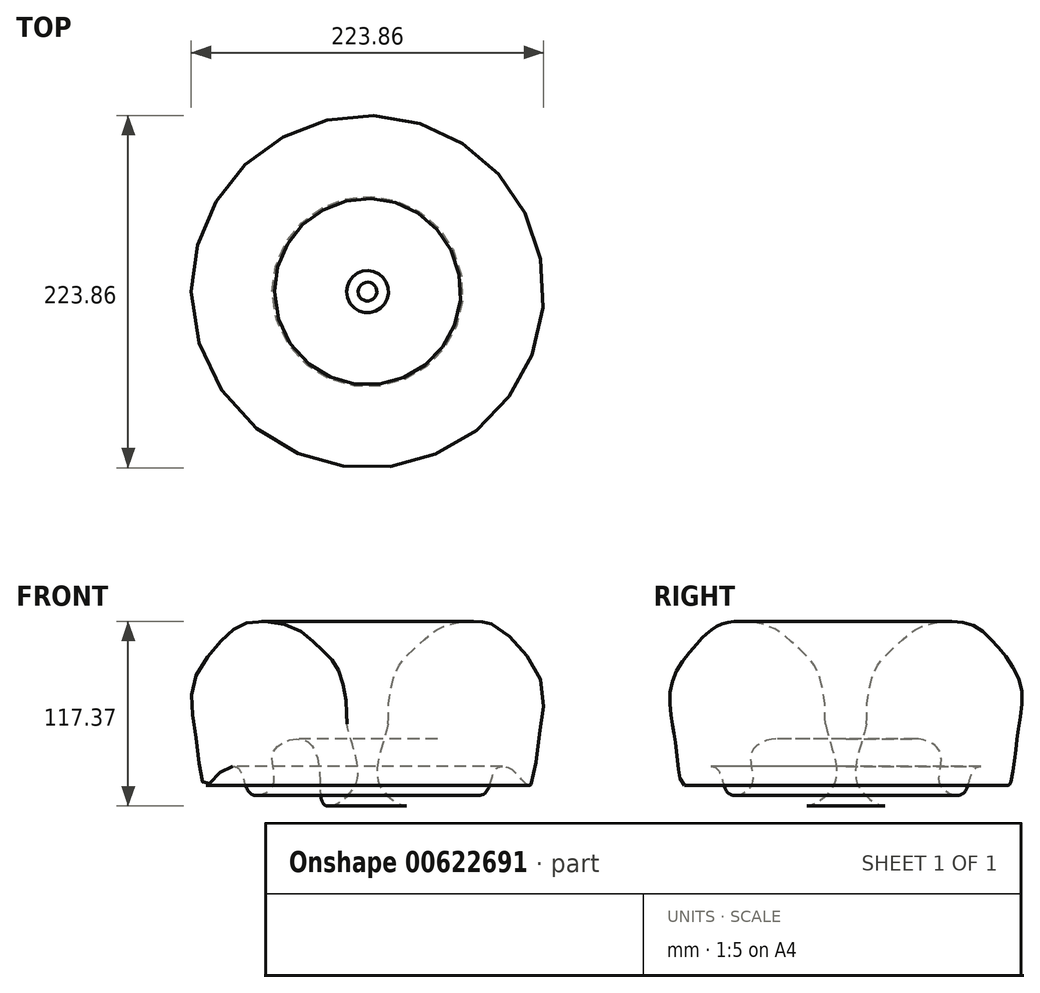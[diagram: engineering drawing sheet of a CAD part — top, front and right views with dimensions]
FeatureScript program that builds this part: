
annotation { "Feature Type Name" : "Feature", "Feature Type Description" : "" }
export const myFeature = defineFeature(function(context is Context, id is Id, definition is map)
    precondition{}
    {
        {
            var Q0;
            Q0=qCreatedBy(makeId("Top.planeOp"),FACE);
            var sketch = newSketch(context, id + "F0", { "sketchPlane" : qUnion([Q0])});
            skCircle(sketch, "E0.cCircle", {"center": v(0, 0) * mm, "radius": 44.85 * mm, "construction": true});
            skLineSegment(sketch, "E0.0", {"start": v(44.98, -25.68) * mm, "end": v(0.25, -51.8) * mm});
            skLineSegment(sketch, "E0.1", {"start": v(0.25, -51.8) * mm, "end": v(-44.73, -26.11) * mm});
            skLineSegment(sketch, "E0.2", {"start": v(-44.73, -26.11) * mm, "end": v(-44.98, 25.68) * mm});
            skLineSegment(sketch, "E0.3", {"start": v(-44.98, 25.68) * mm, "end": v(-0.25, 51.8) * mm});
            skLineSegment(sketch, "E0.4", {"start": v(-0.25, 51.8) * mm, "end": v(44.73, 26.11) * mm});
            skLineSegment(sketch, "E0.5", {"start": v(44.73, 26.11) * mm, "end": v(44.98, -25.68) * mm});
            skPoint(sketch, "E0.0.midPoint", {"position": v(22.61, -38.74) * mm});
            skSolve(sketch);
        }
        {
            var Q0;
            Q0=qCreatedBy(makeId("Front.planeOp"),FACE);
            var sketch = newSketch(context, id + "F1", { "sketchPlane" : qUnion([Q0])});
            skFitSpline(sketch, "E1", {"points": [v(-13.08, 0) * mm, v(-13.28, 9.33) * mm, v(-16.12, 27.99) * mm, v(-22.2, 40.16) * mm, v(-31.74, 49.69) * mm, v(-47.36, 61.45) * mm, v(-75.55, 64.5) * mm, v(-91.37, 54.56) * mm, v(-110.63, 25.96) * mm, v(-108.6, -9.94) * mm, v(-102.93, -38.94) * mm, v(-92.79, -29.81) * mm, v(-81.63, -28.6) * mm, v(-73.93, -44.42) * mm, v(-59.93, -38.74) * mm, v(-59.73, -17.64) * mm, v(-40.06, -10.14) * mm, v(-30.52, -30.02) * mm, v(-26.67, -51.72) * mm, v(-9.84, -42.39) * mm, v(-6.8, -23.32) * mm, v(-13.08, 0) * mm]});
            skSolve(sketch);
        }
        {
            var Q0;
            Q0=makeQuery(id+"F1.imprint","IMPRINT",FACE,{"disambiguationData":[TD([[makeQuery(id+"F1.imprint","IMPRINT",EDGE,{"derivedFrom":sQuery(id+"F1.wireOp",EDGE,"E1")}),1.0]])]});
            var Q1;
            Q1=sQuery(id+"F0.wireOp",EDGE,"E0.cCircle");
            revolve(context, id + "F2", {"entities" : qUnion([Q0]), "axis" : qUnion([Q1]), "revolveType" : RevolveType.FULL});
        }
    });
